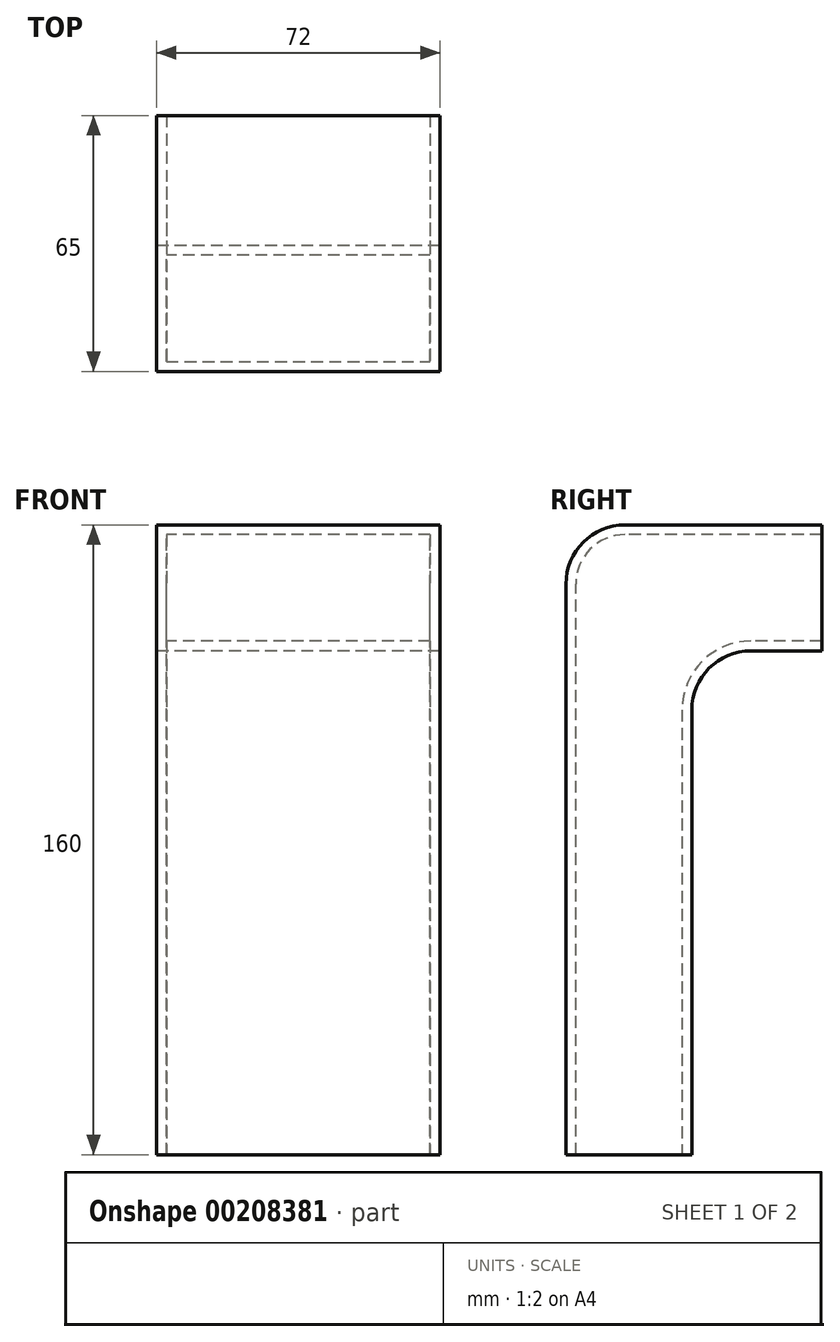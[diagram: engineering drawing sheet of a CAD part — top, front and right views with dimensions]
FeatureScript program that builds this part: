
annotation { "Feature Type Name" : "Feature", "Feature Type Description" : "" }
export const myFeature = defineFeature(function(context is Context, id is Id, definition is map)
    precondition{}
    {
        {
            var Q0;
            Q0=qCreatedBy(makeId("Right.planeOp"),FACE);
            var sketch = newSketch(context, id + "F0", { "sketchPlane" : qUnion([Q0])});
            skLineSegment(sketch, "E0.bottom", {"start": v(0, 0) * mm, "end": v(-28, 0) * mm});
            skLineSegment(sketch, "E0.top", {"start": v(0, 32) * mm, "end": v(-60, 32) * mm});
            skLineSegment(sketch, "E0.left", {"start": v(0, 0) * mm, "end": v(0, 32) * mm});
            skLineSegment(sketch, "E0.right", {"start": v(-60, 0) * mm, "end": v(-60, 32) * mm});
            skLineSegment(sketch, "E1.top", {"start": v(-60, -28) * mm, "end": v(-28, -28) * mm});
            skLineSegment(sketch, "E1.left", {"start": v(-60, 0) * mm, "end": v(-60, -28) * mm});
            skLineSegment(sketch, "E1.right", {"start": v(-28, 0) * mm, "end": v(-28, -28) * mm});
            skSolve(sketch);
        }
        {
            var Q0;
            Q0=makeQuery(id+"F0.imprint","IMPRINT",FACE,{"disambiguationData":[TD([[makeQuery(id+"F0.imprint","IMPRINT",EDGE,{"derivedFrom":sQuery(id+"F0.wireOp",EDGE,"E0.bottom")}),-1.0]])]});
            extrude(context, id + "F1", {"entities" : qUnion([Q0]), "endBound" : BoundingType.SYMMETRIC, "depth" : 72 * mm});
        }
        {
            var Q0;
            Q0=makeQuery(id+"F1.opExtrude","SWEPT_EDGE",EDGE,{"disambiguationData":[OSD([sQuery(id+"F0.wireOp",EDGE,"E0.top"),sQuery(id+"F0.wireOp",EDGE,"E0.right")])]});
            var Q1;
            Q1=makeQuery(id+"F1.opExtrude","SWEPT_EDGE",EDGE,{"disambiguationData":[OSD([sQuery(id+"F0.wireOp",EDGE,"E0.bottom"),sQuery(id+"F0.wireOp",EDGE,"E1.right")])]});
            fillet(context, id + "F2", {"entities" : qUnion([Q0, Q1]), "radius" : 15 * mm, "tangentPropagation" : true, "allowEdgeOverflow" : false});
        }
        {
            var Q0;
            Q0=makeQuery(id+"F1.opExtrude","SWEPT_FACE",FACE,{"disambiguationData":[OSD([sQuery(id+"F0.wireOp",EDGE,"E0.left")])]});
            shell(context, id + "F3", {"entities" : qUnion([Q0]), "thickness" : 2.5 * mm});
        }
        {
            var Q0;
            Q0=makeQuery(id+"F1.opExtrude","SWEPT_FACE",FACE,{"disambiguationData":[OSD([sQuery(id+"F0.wireOp",EDGE,"E1.top")])]});
            var sketch = newSketch(context, id + "F4", { "sketchPlane" : qUnion([Q0])});
            skLineSegment(sketch, "E2.bottom", {"start": v(33.5, 57.5) * mm, "end": v(-33.5, 57.5) * mm});
            skLineSegment(sketch, "E2.top", {"start": v(33.5, 30.5) * mm, "end": v(-33.5, 30.5) * mm});
            skLineSegment(sketch, "E2.left", {"start": v(33.5, 57.5) * mm, "end": v(33.5, 30.5) * mm});
            skLineSegment(sketch, "E2.right", {"start": v(-33.5, 57.5) * mm, "end": v(-33.5, 30.5) * mm});
            skSolve(sketch);
        }
        {
            var Q0;
            Q0=makeQuery(id+"F4.imprint","IMPRINT",FACE,{"disambiguationData":[TD([[makeQuery(id+"F4.imprint","IMPRINT",EDGE,{"derivedFrom":sQuery(id+"F4.wireOp",EDGE,"E2.bottom")}),1.0]])]});
            extrude(context, id + "F5", {"entities" : qUnion([Q0]), "operationType" : NewBodyOperationType.REMOVE, "oppositeDirection" : true, "depth" : 3 * mm});
        }
        {
            var Q0;
            Q0=makeQuery(id+"F1.opExtrude","SWEPT_FACE",FACE,{"disambiguationData":[OSD([sQuery(id+"F0.wireOp",EDGE,"E1.top")])]});
            extrude(context, id + "F6", {"entities" : qUnion([Q0]), "operationType" : NewBodyOperationType.ADD, "depth" : 100 * mm});
        }
        {
            var Q0;
            Q0=makeQuery(id+"F1.opExtrude","SWEPT_FACE",FACE,{"disambiguationData":[OSD([sQuery(id+"F0.wireOp",EDGE,"E0.left")])]});
            extrude(context, id + "F7", {"entities" : qUnion([Q0]), "operationType" : NewBodyOperationType.ADD, "depth" : 5 * mm});
        }
    });
